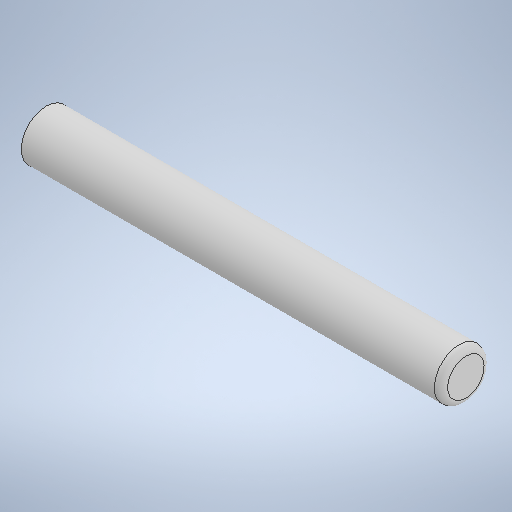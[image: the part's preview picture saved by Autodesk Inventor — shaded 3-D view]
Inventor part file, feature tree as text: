
AUTODESK INVENTOR PART (.ipt)
format: ipt  version: 2025 (Build 290162000, 162)  size: 247,808 bytes
history: native  units: in
note: dims shown in document units (in); Inventor stores cm internally (conversion verified against a paired STEP export)
features: sketch x2, revolve x1, extrude x1, fillet x1
ambient origin geometry x8: Origin, YZ Plane, XZ Plane, XY Plane, X Axis, Y Axis, Z Axis, Center Point
bodies: Solid1 (feature_tree)
feature tree (5):
  revolve  "Revolution1"  [1 undecoded]
  extrude  "Extrusion2"  Depth=0.0787in
  fillet  "Fillet1"  Radius=0.3205in
  sketch  "Sketch1"  dims[d0=3.937in d2=0.2953in]
  sketch  "Sketch3"  dims[d3=90.0deg d8=0.0787in d9=0.3205in d10=0.126in d11=0.0in d12=0.0394in]
note: 1 required parameter value undecoded (feature->parameter linkage not recoverable at this tier; creation-order binding heuristic only, values carry confidence <= 0.55)
